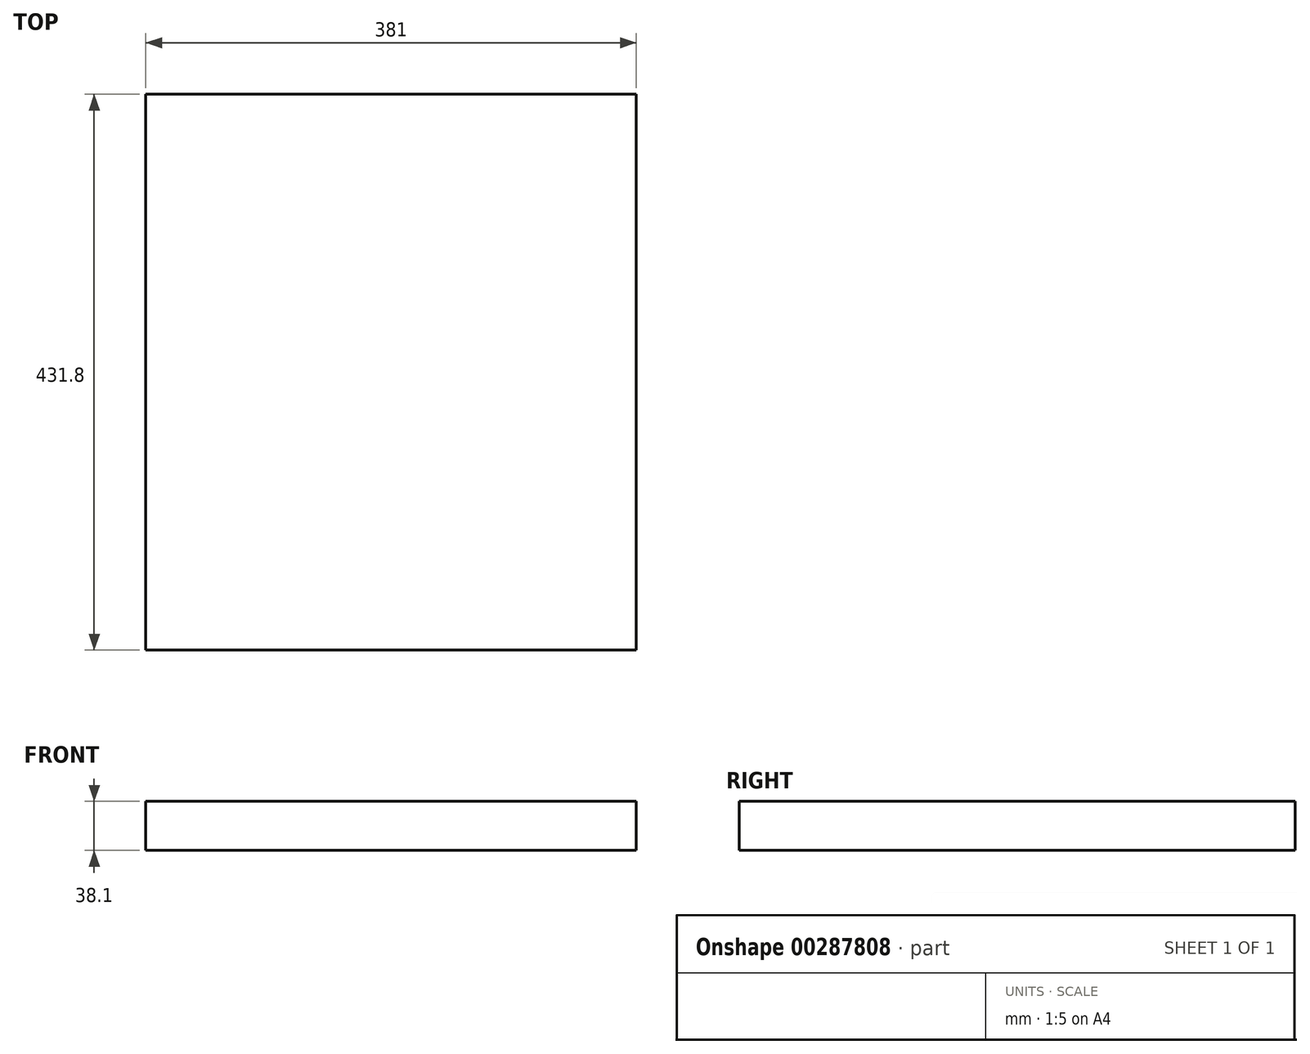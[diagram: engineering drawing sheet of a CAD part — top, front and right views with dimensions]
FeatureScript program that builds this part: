
annotation { "Feature Type Name" : "Feature", "Feature Type Description" : "" }
export const myFeature = defineFeature(function(context is Context, id is Id, definition is map)
    precondition{}
    {
        {
            var Q0;
            Q0=qCreatedBy(makeId("Top.planeOp"),FACE);
            var sketch = newSketch(context, id + "F0", { "sketchPlane" : qUnion([Q0])});
            skLineSegment(sketch, "E0.bottom", {"start": v(0, 0) * mm, "end": v(-381, 0) * mm});
            skLineSegment(sketch, "E0.top", {"start": v(0, 431.8) * mm, "end": v(-381, 431.8) * mm});
            skLineSegment(sketch, "E0.left", {"start": v(0, 0) * mm, "end": v(0, 431.8) * mm});
            skLineSegment(sketch, "E0.right", {"start": v(-381, 0) * mm, "end": v(-381, 431.8) * mm});
            skSolve(sketch);
        }
        {
            var Q0;
            Q0=makeQuery(id+"F0.imprint","IMPRINT",FACE,{"disambiguationData":[TD([[makeQuery(id+"F0.imprint","IMPRINT",EDGE,{"derivedFrom":sQuery(id+"F0.wireOp",EDGE,"E0.bottom")}),-1.0]])]});
            extrude(context, id + "F1", {"entities" : qUnion([Q0]), "depth" : 38.1 * mm});
        }
    });
